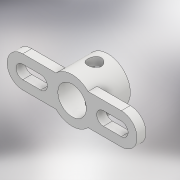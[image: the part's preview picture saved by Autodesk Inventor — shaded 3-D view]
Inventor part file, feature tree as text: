
AUTODESK INVENTOR PART (.ipt)
format: ipt  version: 2018.2 (Build 222227000, 227)  size: 171,008 bytes
history: native  units: mm
features: extrude x3, plane x1, sketch x1
ambient origin geometry x8: Origin, YZ Plane, XZ Plane, XY Plane, X Axis, Y Axis, Z Axis, Center Point
bodies: Solid1 (feature_tree)
feature tree (5):
  extrude  "Extrusion1"  Depth=10.0mm
  extrude  "Extrusion2"  Depth=3.0mm
  extrude  "Extrusion3"  Depth=3.0mm TaperAngle=0.0deg
  plane  "Work Plane1"
  sketch  "Sketch2"  dims[d0=6.35mm d1=10.0mm d6=3.5mm d7=2.0mm d8=0.0mm d9=6.0mm d10=0.0mm d11=3.0mm d12=6.0mm d13=0.0mm d15=3.0mm d16=4.0mm d17=7.0mm]
